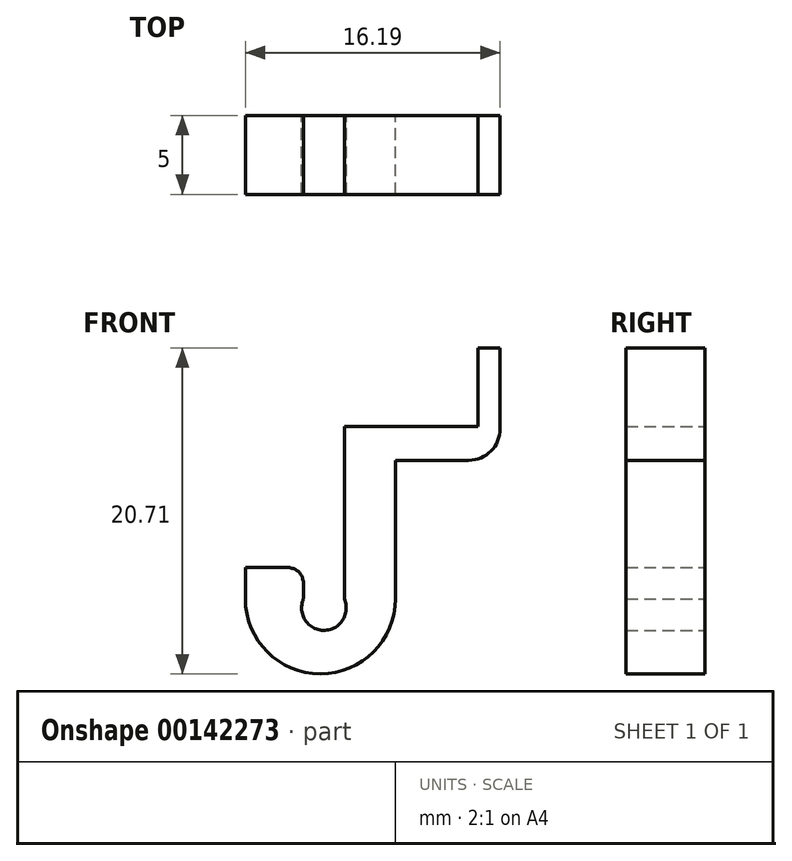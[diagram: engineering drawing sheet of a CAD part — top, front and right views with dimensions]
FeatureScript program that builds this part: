
annotation { "Feature Type Name" : "Feature", "Feature Type Description" : "" }
export const myFeature = defineFeature(function(context is Context, id is Id, definition is map)
    precondition{}
    {
        {
            var Q0;
            Q0=qCreatedBy(makeId("Front.planeOp"),FACE);
            var sketch = newSketch(context, id + "F0", { "sketchPlane" : qUnion([Q0])});
            skLineSegment(sketch, "E0", {"start": v(1.42, 30.7) * mm, "end": v(1.42, 23.57) * mm});
            skLineSegment(sketch, "E1", {"start": v(1.42, 23.57) * mm, "end": v(-5.23, 23.57) * mm});
            skLineSegment(sketch, "E2", {"start": v(-5.23, 23.57) * mm, "end": v(-5.23, 14.77) * mm});
            skArc(sketch, "E3", {"start": v(-5.23, 14.77) * mm, "mid": v(-10, 10) * mm, "end": v(-14.77, 14.77) * mm});
            skLineSegment(sketch, "E4", {"start": v(-14.77, 14.77) * mm, "end": v(-11.07, 14.77) * mm});
            skArc(sketch, "E5", {"start": v(-11.07, 14.77) * mm, "mid": v(-9.78, 12.76) * mm, "end": v(-8.48, 14.77) * mm});
            skLineSegment(sketch, "E6", {"start": v(-8.48, 14.77) * mm, "end": v(-8.48, 25.7) * mm});
            skLineSegment(sketch, "E7", {"start": v(-8.48, 25.7) * mm, "end": v(0, 25.7) * mm});
            skLineSegment(sketch, "E8", {"start": v(0, 25.7) * mm, "end": v(0, 29.08) * mm});
            skLineSegment(sketch, "E9", {"start": v(0, 29.08) * mm, "end": v(0, 30.7) * mm});
            skLineSegment(sketch, "E10", {"start": v(1.42, 30.7) * mm, "end": v(0, 30.7) * mm});
            skSolve(sketch);
        }
        {
            var Q0;
            Q0=makeQuery(id+"F0.imprint","IMPRINT",FACE,{"disambiguationData":[TD([[makeQuery(id+"F0.imprint","IMPRINT",EDGE,{"derivedFrom":sQuery(id+"F0.wireOp",EDGE,"E0")}),-1.0]])]});
            extrude(context, id + "F1", {"entities" : qUnion([Q0]), "depth" : 5 * mm});
        }
        {
            var Q0;
            Q0=makeQuery(id+"F1.opExtrude","SWEPT_EDGE",EDGE,{"disambiguationData":[OSD([sQuery(id+"F0.wireOp",EDGE,"E0"),sQuery(id+"F0.wireOp",EDGE,"E1")])]});
            fillet(context, id + "F2", {"entities" : qUnion([Q0]), "radius" : 2 * mm, "tangentPropagation" : true, "allowEdgeOverflow" : false});
        }
        {
            var Q0;
            Q0=makeQuery(id+"F1.opExtrude","SWEPT_FACE",FACE,{"disambiguationData":[OSD([sQuery(id+"F0.wireOp",EDGE,"E4")])]});
            extrude(context, id + "F3", {"entities" : qUnion([Q0]), "operationType" : NewBodyOperationType.ADD, "depth" : 2 * mm});
        }
        {
            var Q0;
            Q0=makeQuery(id+"F3.opExtrude","CAP_EDGE",EDGE,{"disambiguationData":[OSD([sQuery(id+"F0.wireOp",EDGE,"E4"),sQuery(id+"F0.wireOp",EDGE,"E5")])],"isStart":false});
            var Q1;
            {var subQ0=sQuery(id+"F0.wireOp",EDGE,"E5");var subQ1=sQuery(id+"F0.wireOp",EDGE,"E4");Q1=makeQuery(id+"F3.boolean.opBoolean","MERGE",EDGE,{"derivedFrom":[makeQuery(id+"F1.opExtrude","SWEPT_EDGE",EDGE,{"disambiguationData":[OSD([subQ1,subQ0])]}),makeQuery(id+"F3.opExtrude","CAP_EDGE",EDGE,{"disambiguationData":[OSD([subQ1,subQ0])],"isStart":true})]});}
            fillet(context, id + "F4", {"entities" : qUnion([Q0, Q1]), "radius" : 1.2 * mm, "tangentPropagation" : true, "rho" : 0.5, "crossSection" : FilletCrossSection.CONIC, "allowEdgeOverflow" : false});
        }
    });
